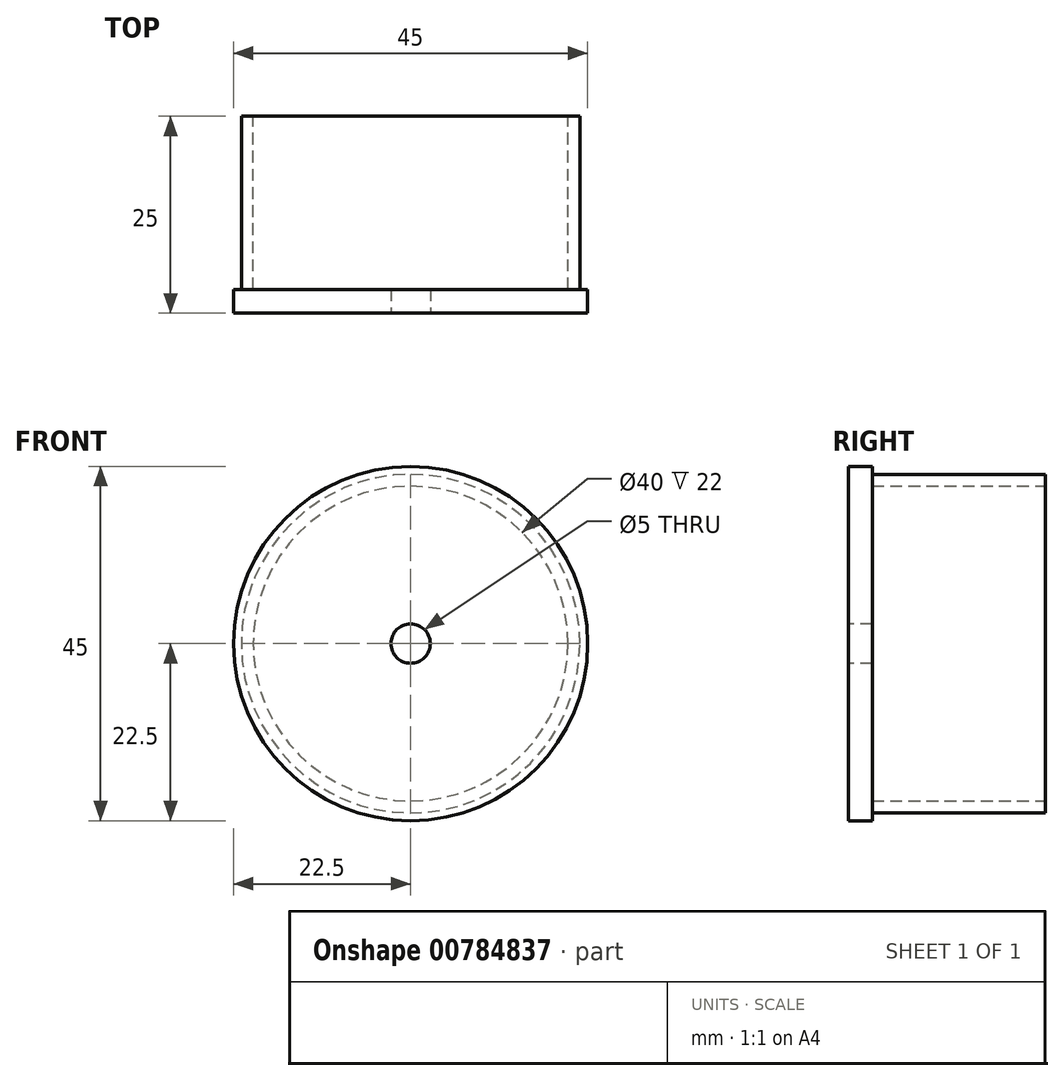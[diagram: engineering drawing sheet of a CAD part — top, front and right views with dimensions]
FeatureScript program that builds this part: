
annotation { "Feature Type Name" : "Feature", "Feature Type Description" : "" }
export const myFeature = defineFeature(function(context is Context, id is Id, definition is map)
    precondition{}
    {
        {
            var Q0;
            Q0=qCreatedBy(makeId("Front.planeOp"),FACE);
            var sketch = newSketch(context, id + "F0", { "sketchPlane" : qUnion([Q0])});
            skCircle(sketch, "E0", {"center": v(0, 0) * mm, "radius": 20 * mm});
            skCircle(sketch, "E1", {"center": v(0, 0) * mm, "radius": 21.5 * mm});
            skSolve(sketch);
        }
        {
            var Q0;
            Q0 = qSketchRegion(id + "F0", true);
            extrude(context, id + "F1", {"entities" : qUnion([Q0]), "depth" : 22 * mm, "offsetDistance" : 25 * mm});
        }
        {
            var Q0;
            Q0=makeQuery(id+"F1.opExtrude","CAP_FACE",FACE,{"disambiguationData":[OSD([sQuery(id+"F0.wireOp",EDGE,"E0"),sQuery(id+"F0.wireOp",EDGE,"E1")])],"isStart":false});
            var sketch = newSketch(context, id + "F2", { "sketchPlane" : qUnion([Q0])});
            skCircle(sketch, "E2", {"center": v(0, 0) * mm, "radius": 22.5 * mm});
            skSolve(sketch);
        }
        {
            var Q0;
            Q0 = qSketchRegion(id + "F2", true);
            extrude(context, id + "F3", {"entities" : qUnion([Q0]), "operationType" : NewBodyOperationType.ADD, "depth" : 3 * mm, "offsetDistance" : 25 * mm});
        }
        {
            var Q0;
            Q0=makeQuery(id+"F3.opExtrude","CAP_FACE",FACE,{"disambiguationData":[OSD([sQuery(id+"F2.wireOp",EDGE,"E2")])],"isStart":false});
            var sketch = newSketch(context, id + "F4", { "sketchPlane" : qUnion([Q0])});
            skCircle(sketch, "E3", {"center": v(0, 0) * mm, "radius": 2.5 * mm});
            skSolve(sketch);
        }
        {
            var Q0;
            Q0=makeQuery(id+"F4.imprint","IMPRINT",FACE,{"disambiguationData":[TD([[makeQuery(id+"F4.imprint","IMPRINT",EDGE,{"derivedFrom":sQuery(id+"F4.wireOp",EDGE,"E3")}),1.0]])]});
            var Q1;
            Q1=sQuery(id+"F4.wireOp",EDGE,"E3");
            extrude(context, id + "F5", {"entities" : qUnion([Q0]), "operationType" : NewBodyOperationType.REMOVE, "surfaceEntities" : qUnion([Q1]), "oppositeDirection" : true, "depth" : 3 * mm, "offsetDistance" : 25 * mm});
        }
    });
